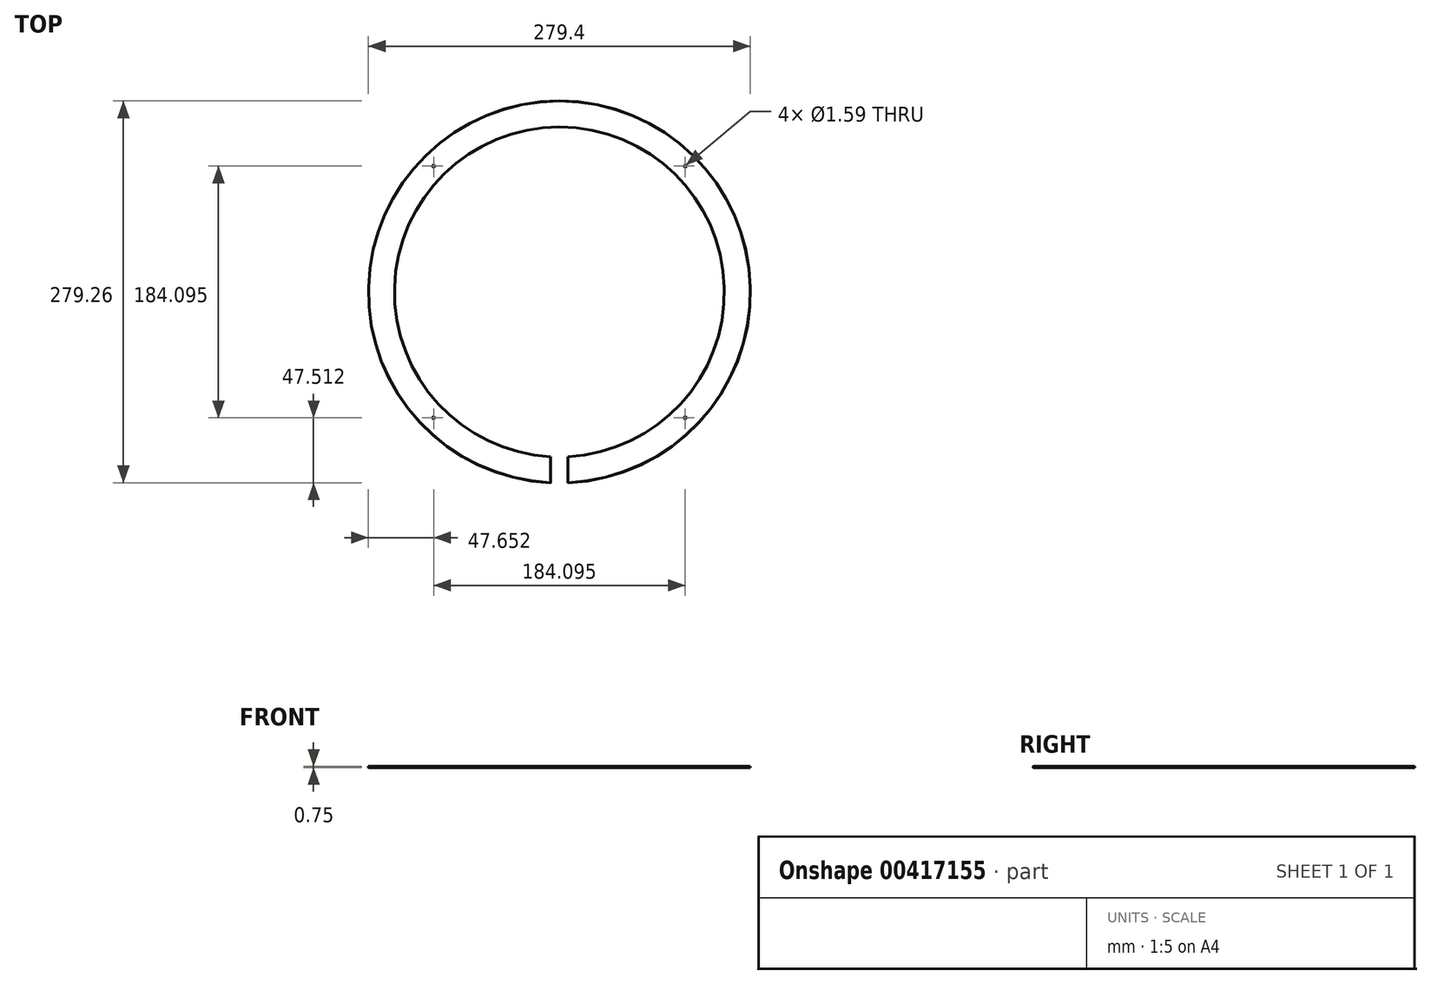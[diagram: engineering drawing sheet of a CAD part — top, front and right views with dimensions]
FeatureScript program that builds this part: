
annotation { "Feature Type Name" : "Feature", "Feature Type Description" : "" }
export const myFeature = defineFeature(function(context is Context, id is Id, definition is map)
    precondition{}
    {
        {
            assignVariable(context, id + "F0", {"name" : "BaseThickness", "anyValue" : 0.75});
        }
        {
            assignVariable(context, id + "F1", {"name" : "OuterChamfer", "anyValue" : 0.06});
        }
        {
            var Q0;
            Q0=qCreatedBy(makeId("Top.planeOp"),FACE);
            var sketch = newSketch(context, id + "F2", { "sketchPlane" : qUnion([Q0])});
            skCircle(sketch, "E0", {"center": v(0, 0) * mm, "radius": 139.7 * mm});
            skSolve(sketch);
        }
        {
            var Q0;
            Q0=qSketchRegion(id+"F2",true);
            extrude(context, id + "F3", {"entities" : qUnion([Q0]), "depth" : (getVariable(context, 'BaseThickness')) * mm});
        }
        {
            var Q0;
            Q0=makeQuery(id+"F3.opExtrude","CAP_EDGE",EDGE,{"disambiguationData":[OSD([sQuery(id+"F2.wireOp",EDGE,"E0")])],"isStart":false});
            var Q1;
            Q1=makeQuery(id+"F3.opExtrude","CAP_EDGE",EDGE,{"disambiguationData":[OSD([sQuery(id+"F2.wireOp",EDGE,"E0")])],"isStart":true});
            chamfer(context, id + "F4", {"entities" : qUnion([Q0, Q1]), "width" : (getVariable(context, 'OuterChamfer')) * mm, "tangentPropagation" : true});
        }
        {
            var Q0;
            Q0=makeQuery(id+"F3.opExtrude","CAP_FACE",FACE,{"disambiguationData":[OSD([sQuery(id+"F2.wireOp",EDGE,"E0")])],"isStart":true});
            var sketch = newSketch(context, id + "F5", { "sketchPlane" : qUnion([Q0])});
            skCircle(sketch, "E1", {"center": v(0, 0) * mm, "radius": 120.65 * mm});
            skSolve(sketch);
        }
        {
            var Q0;
            Q0=makeQuery(id+"F5.imprint","IMPRINT",FACE,{"disambiguationData":[TD([[makeQuery(id+"F5.imprint","IMPRINT",EDGE,{"derivedFrom":sQuery(id+"F5.wireOp",EDGE,"E1")}),1.0]])]});
            extrude(context, id + "F6", {"entities" : qUnion([Q0]), "operationType" : NewBodyOperationType.REMOVE, "endBound" : BoundingType.THROUGH_ALL, "oppositeDirection" : true, "depth" : 25.4 * mm});
        }
        {
            var Q0;
            Q0=qCreatedBy(makeId("Front.planeOp"),FACE);
            var sketch = newSketch(context, id + "F7", { "sketchPlane" : qUnion([Q0])});
            skLineSegment(sketch, "E2.bottom", {"start": v(-6.35, 0) * mm, "end": v(6.35, 0) * mm});
            skLineSegment(sketch, "E2.top", {"start": v(-6.35, 5.56) * mm, "end": v(6.35, 5.56) * mm});
            skLineSegment(sketch, "E2.left", {"start": v(-6.35, 0) * mm, "end": v(-6.35, 5.56) * mm});
            skLineSegment(sketch, "E2.right", {"start": v(6.35, 0) * mm, "end": v(6.35, 5.56) * mm});
            skSolve(sketch);
        }
        {
            var Q0;
            Q0=makeQuery(id+"F7.imprint","IMPRINT",FACE,{"disambiguationData":[TD([[makeQuery(id+"F7.imprint","IMPRINT",EDGE,{"derivedFrom":sQuery(id+"F7.wireOp",EDGE,"E2.bottom")}),1.0]])]});
            extrude(context, id + "F8", {"entities" : qUnion([Q0]), "operationType" : NewBodyOperationType.REMOVE, "endBound" : BoundingType.THROUGH_ALL, "depth" : 139.7 * mm});
        }
        {
            var Q0;
            Q0=qCreatedBy(makeId("Top.planeOp"),FACE);
            var sketch = newSketch(context, id + "F9", { "sketchPlane" : qUnion([Q0])});
            skLineSegment(sketch, "E3", {"start": v(0, 0) * mm, "end": v(168.97, 0) * mm, "construction": true});
            skLineSegment(sketch, "E4", {"start": v(0, 0) * mm, "end": v(92.05, -92.05) * mm, "construction": true});
            skCircle(sketch, "E5", {"center": v(92.05, -92.05) * mm, "radius": 0.8 * mm});
            skCircle(sketch, "E6.1.0", {"center": v(-92.05, -92.05) * mm, "radius": 0.8 * mm});
            skCircle(sketch, "E6.2.0", {"center": v(-92.05, 92.05) * mm, "radius": 0.8 * mm});
            skCircle(sketch, "E6.3.0", {"center": v(92.05, 92.05) * mm, "radius": 0.8 * mm});
            skPoint(sketch, "E6.center", {"position": v(0, 0) * mm});
            skLineSegment(sketch, "E6.anchor2", {"start": v(0, 0) * mm, "end": v(92.05, 92.05) * mm, "construction": true});
            skSolve(sketch);
        }
        {
            var Q0;
            Q0=makeQuery(id+"F9.imprint","IMPRINT",FACE,{"disambiguationData":[TD([[makeQuery(id+"F9.imprint","IMPRINT",EDGE,{"derivedFrom":sQuery(id+"F9.wireOp",EDGE,"E5")}),1.0]])]});
            var Q1;
            Q1=makeQuery(id+"F9.imprint","IMPRINT",FACE,{"disambiguationData":[TD([[makeQuery(id+"F9.imprint","IMPRINT",EDGE,{"derivedFrom":sQuery(id+"F9.wireOp",EDGE,"E6.1.0")}),1.0]])]});
            var Q2;
            Q2=makeQuery(id+"F9.imprint","IMPRINT",FACE,{"disambiguationData":[TD([[makeQuery(id+"F9.imprint","IMPRINT",EDGE,{"derivedFrom":sQuery(id+"F9.wireOp",EDGE,"E6.2.0")}),1.0]])]});
            var Q3;
            Q3=makeQuery(id+"F9.imprint","IMPRINT",FACE,{"disambiguationData":[TD([[makeQuery(id+"F9.imprint","IMPRINT",EDGE,{"derivedFrom":sQuery(id+"F9.wireOp",EDGE,"E6.3.0")}),1.0]])]});
            extrude(context, id + "F10", {"entities" : qUnion([Q0, Q1, Q2, Q3]), "operationType" : NewBodyOperationType.REMOVE, "endBound" : BoundingType.THROUGH_ALL, "depth" : 25.4 * mm});
        }
    });
